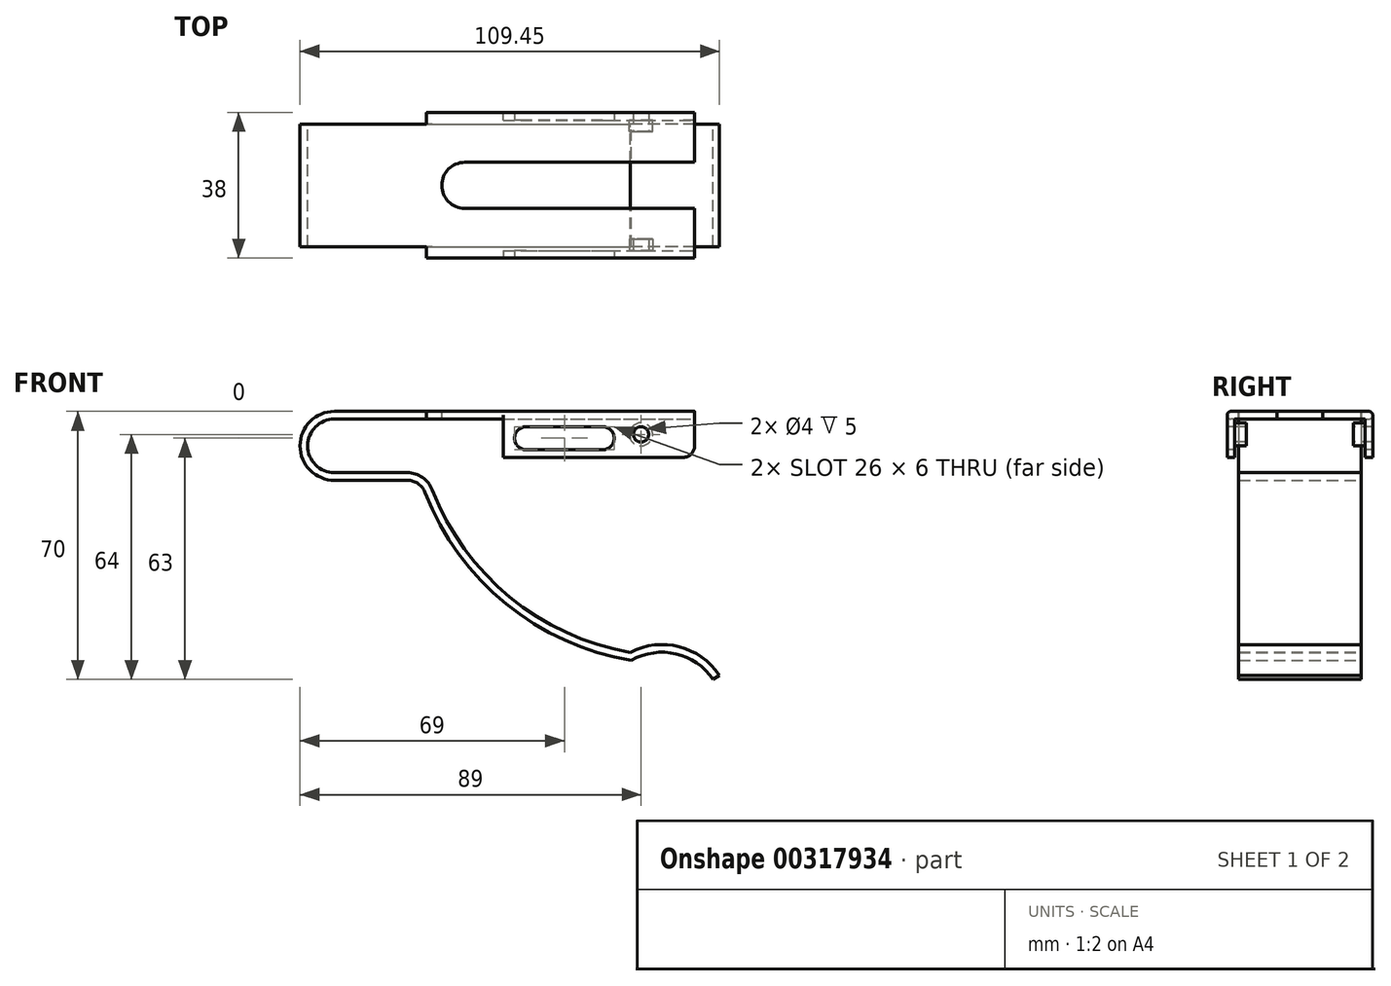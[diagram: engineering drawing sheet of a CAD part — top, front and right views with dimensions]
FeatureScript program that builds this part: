
annotation { "Feature Type Name" : "Feature", "Feature Type Description" : "" }
export const myFeature = defineFeature(function(context is Context, id is Id, definition is map)
    precondition{}
    {
        {
            var Q0;
            Q0=qCreatedBy(makeId("Front.planeOp"),FACE);
            var sketch = newSketch(context, id + "F0", { "sketchPlane" : qUnion([Q0])});
            skArc(sketch, "E0", {"start": v(0, 9) * mm, "mid": v(-9, 0) * mm, "end": v(0, -9) * mm});
            skLineSegment(sketch, "E1", {"start": v(0, 9) * mm, "end": v(94, 9) * mm});
            skLineSegment(sketch, "E2", {"start": v(0, -9) * mm, "end": v(19, -9) * mm});
            skArc(sketch, "E3", {"start": v(23.66, -12.2) * mm, "mid": v(44.77, -41.24) * mm, "end": v(77.5, -56) * mm});
            skArc(sketch, "E4", {"start": v(98.78, -61) * mm, "mid": v(89.13, -54.3) * mm, "end": v(77.5, -56) * mm});
            skPoint(sketch, "E5.visualSharp", {"position": v(22.52, -9) * mm});
            skArc(sketch, "E5.filletArc", {"start": v(23.66, -12.2) * mm, "mid": v(21.83, -9.88) * mm, "end": v(19, -9) * mm});
            skLineSegment(sketch, "E6.0", {"start": v(0, 7) * mm, "end": v(94, 7) * mm});
            skArc(sketch, "E6.1", {"start": v(0, 7) * mm, "mid": v(-7, 0) * mm, "end": v(0, -7) * mm});
            skArc(sketch, "E6.2", {"start": v(100.45, -59.9) * mm, "mid": v(89.94, -52.44) * mm, "end": v(77.15, -53.91) * mm});
            skArc(sketch, "E6.3", {"start": v(25.53, -11.47) * mm, "mid": v(45.77, -39.47) * mm, "end": v(77.15, -53.91) * mm});
            skArc(sketch, "E6.4", {"start": v(25.53, -11.47) * mm, "mid": v(22.96, -8.23) * mm, "end": v(19, -7) * mm});
            skLineSegment(sketch, "E6.5", {"start": v(0, -7) * mm, "end": v(19, -7) * mm});
            skLineSegment(sketch, "E7", {"start": v(94, 9) * mm, "end": v(94, 7) * mm});
            skLineSegment(sketch, "E8", {"start": v(100.45, -59.9) * mm, "end": v(98.78, -61) * mm});
            skSolve(sketch);
        }
        {
            var Q0;
            Q0=qSketchRegion(id+"F0",true);
            extrude(context, id + "F1", {"entities" : qUnion([Q0]), "depth" : 16 * mm});
        }
        {
            var Q0;
            Q0=makeQuery(id+"F1.opExtrude","SWEPT_FACE",FACE,{"disambiguationData":[OSD([sQuery(id+"F0.wireOp",EDGE,"E1")])]});
            var sketch = newSketch(context, id + "F2", { "sketchPlane" : qUnion([Q0])});
            skLineSegment(sketch, "E9.bottom", {"start": v(79.88, -16) * mm, "end": v(24, -16) * mm});
            skLineSegment(sketch, "E9.top", {"start": v(94, -19) * mm, "end": v(24, -19) * mm});
            skLineSegment(sketch, "E9.left", {"start": v(94, -16) * mm, "end": v(94, -19) * mm});
            skLineSegment(sketch, "E9.right", {"start": v(24, -16) * mm, "end": v(24, -19) * mm});
            skLineSegment(sketch, "E10.top", {"start": v(94, -10.87) * mm, "end": v(79.88, -10.87) * mm});
            skLineSegment(sketch, "E10.left", {"start": v(94, -16) * mm, "end": v(94, -10.87) * mm});
            skLineSegment(sketch, "E10.right", {"start": v(79.88, -16) * mm, "end": v(79.88, -10.87) * mm});
            skSolve(sketch);
        }
        {
            var Q0;
            Q0=makeQuery(id+"F2.imprint","IMPRINT",FACE,{"disambiguationData":[TD([[makeQuery(id+"F2.imprint","IMPRINT",EDGE,{"derivedFrom":sQuery(id+"F2.wireOp",EDGE,"E10.top")}),1.0]])]});
            var Q1;
            {var subQ1=sQuery(id+"F2.wireOp",EDGE,"E9.bottom");Q1=makeQuery(id+"F2.imprint","IMPRINT",FACE,{"disambiguationData":[TD([[makeQuery(id+"F2.imprint","IMPRINT",EDGE,{"derivedFrom":subQ1}),-1.0]])]});}
            extrude(context, id + "F3", {"entities" : qUnion([Q0, Q1]), "operationType" : NewBodyOperationType.ADD, "oppositeDirection" : true, "depth" : 2 * mm});
        }
        {
            var Q0;
            Q0=makeQuery(id+"F3.opExtrude","SWEPT_FACE",FACE,{"disambiguationData":[OSD([sQuery(id+"F2.wireOp",EDGE,"E9.top")])]});
            var sketch = newSketch(context, id + "F4", { "sketchPlane" : qUnion([Q0])});
            skPoint(sketch, "E11", {"position": v(94, -3) * mm});
            skPoint(sketch, "E11.positionSnap0", {"position": v(94, 8) * mm});
            skPoint(sketch, "E12", {"position": v(94, 9) * mm});
            skLineSegment(sketch, "E13.bottom", {"start": v(44, 9) * mm, "end": v(94, 9) * mm});
            skLineSegment(sketch, "E13.top", {"start": v(44, -3) * mm, "end": v(94, -3) * mm});
            skLineSegment(sketch, "E13.left", {"start": v(44, 9) * mm, "end": v(44, -3) * mm});
            skLineSegment(sketch, "E13.right", {"start": v(94, 9) * mm, "end": v(94, -3) * mm});
            skSolve(sketch);
        }
        {
            var Q0;
            Q0=qSketchRegion(id+"F4",true);
            extrude(context, id + "F5", {"entities" : qUnion([Q0]), "operationType" : NewBodyOperationType.ADD, "oppositeDirection" : true, "depth" : 2 * mm});
        }
        {
            var Q0;
            Q0=makeQuery(id+"F3.opExtrude","CAP_EDGE",EDGE,{"disambiguationData":[OSD([sQuery(id+"F2.wireOp",EDGE,"E9.top")])],"isStart":true});
            var Q1;
            Q1=makeQuery(id+"F3.opExtrude","CAP_EDGE",EDGE,{"disambiguationData":[OSD([sQuery(id+"F2.wireOp",EDGE,"E9.top")])],"isStart":false});
            fillet(context, id + "F6", {"entities" : qUnion([Q0, Q1]), "radius" : 1 * mm, "tangentPropagation" : true, "allowEdgeOverflow" : false});
        }
        {
            var Q0;
            Q0=makeQuery(id+"F1.opExtrude","SWEPT_BODY",BODY,{"disambiguationData":[OSD([sQuery(id+"F0.wireOp",EDGE,"E0"),sQuery(id+"F0.wireOp",EDGE,"E1"),sQuery(id+"F0.wireOp",EDGE,"E2"),sQuery(id+"F0.wireOp",EDGE,"E3"),sQuery(id+"F0.wireOp",EDGE,"E4"),sQuery(id+"F0.wireOp",EDGE,"E5.filletArc"),sQuery(id+"F0.wireOp",EDGE,"E6.0"),sQuery(id+"F0.wireOp",EDGE,"E6.1"),sQuery(id+"F0.wireOp",EDGE,"E6.2"),sQuery(id+"F0.wireOp",EDGE,"E6.3"),sQuery(id+"F0.wireOp",EDGE,"E6.4"),sQuery(id+"F0.wireOp",EDGE,"E6.5"),sQuery(id+"F0.wireOp",EDGE,"E7"),sQuery(id+"F0.wireOp",EDGE,"E8")])]});
            var Q1;
            Q1=qCreatedBy(makeId("Front.planeOp"),FACE);
            mirror(context, id + "F7", {"operationType" : NewBodyOperationType.ADD, "entities" : qUnion([Q0]), "mirrorPlane" : qUnion([Q1])});
        }
        {
            var Q0;
            {var subQ0=makeQuery(id+"F3.boolean.opBoolean","MERGE",FACE,{"derivedFrom":[makeQuery(id+"F1.opExtrude","SWEPT_FACE",FACE,{"disambiguationData":[OSD([sQuery(id+"F0.wireOp",EDGE,"E1")])]}),makeQuery(id+"F3.opExtrude","CAP_FACE",FACE,{"disambiguationData":[OSD([sQuery(id+"F2.wireOp",EDGE,"E9.bottom"),sQuery(id+"F2.wireOp",EDGE,"E9.top"),sQuery(id+"F2.wireOp",EDGE,"E9.left"),sQuery(id+"F2.wireOp",EDGE,"E9.right"),sQuery(id+"F2.wireOp",EDGE,"E10.top"),sQuery(id+"F2.wireOp",EDGE,"E10.left"),sQuery(id+"F2.wireOp",EDGE,"E10.right")])],"isStart":true})]});Q0=makeQuery(id+"F7.boolean.opBoolean","MERGE",FACE,{"derivedFrom":[subQ0,makeQuery(id+"F7.opPattern","COPY",FACE,{"derivedFrom":subQ0,"instanceName":"1"})]});}
            var sketch = newSketch(context, id + "F8", { "sketchPlane" : qUnion([Q0])});
            skPoint(sketch, "E14", {"position": v(0, 0) * mm});
            skArc(sketch, "E15", {"start": v(34, 6) * mm, "mid": v(28, 0) * mm, "end": v(34, -6) * mm});
            skPoint(sketch, "E16", {"position": v(34, 6) * mm});
            skLineSegment(sketch, "E17", {"start": v(34, 6) * mm, "end": v(94, 6) * mm});
            skPoint(sketch, "E18", {"position": v(34, -6) * mm});
            skLineSegment(sketch, "E19", {"start": v(94, 6) * mm, "end": v(94, -6) * mm});
            skLineSegment(sketch, "E20", {"start": v(94, -6) * mm, "end": v(34, -6) * mm});
            skSolve(sketch);
        }
        {
            var Q0;
            Q0=qSketchRegion(id+"F8",true);
            extrude(context, id + "F9", {"entities" : qUnion([Q0]), "operationType" : NewBodyOperationType.REMOVE, "oppositeDirection" : true, "depth" : 2 * mm});
        }
        {
            var Q0;
            Q0=makeQuery(id+"F5.boolean.opBoolean","MERGE",FACE,{"derivedFrom":[makeQuery(id+"F3.opExtrude","SWEPT_FACE",FACE,{"disambiguationData":[OSD([sQuery(id+"F2.wireOp",EDGE,"E9.top")])]}),makeQuery(id+"F5.opExtrude","CAP_FACE",FACE,{"disambiguationData":[OSD([sQuery(id+"F4.wireOp",EDGE,"E13.bottom"),sQuery(id+"F4.wireOp",EDGE,"E13.top"),sQuery(id+"F4.wireOp",EDGE,"E13.left"),sQuery(id+"F4.wireOp",EDGE,"E13.right")])],"isStart":true})]});
            var sketch = newSketch(context, id + "F10", { "sketchPlane" : qUnion([Q0])});
            skLineSegment(sketch, "E21", {"start": v(50, 2) * mm, "end": v(70, 2) * mm});
            skArc(sketch, "E22.0.startCap", {"start": v(50, -1) * mm, "mid": v(47, 2) * mm, "end": v(50, 5) * mm});
            skArc(sketch, "E22.0.endCap", {"start": v(70, 5) * mm, "mid": v(73, 2) * mm, "end": v(70, -1) * mm});
            skLineSegment(sketch, "E22.0.left", {"start": v(50, 5) * mm, "end": v(70, 5) * mm});
            skLineSegment(sketch, "E22.0.right", {"start": v(50, -1) * mm, "end": v(70, -1) * mm});
            skSolve(sketch);
        }
        {
            var Q0;
            Q0=qSketchRegion(id+"F10",true);
            extrude(context, id + "F11", {"entities" : qUnion([Q0]), "operationType" : NewBodyOperationType.ADD, "endBound" : BoundingType.THROUGH_ALL, "depth" : 25 * mm});
        }
        {
            var Q0;
            Q0=makeQuery(id+"F5.boolean.opBoolean","MERGE",FACE,{"derivedFrom":[makeQuery(id+"F3.opExtrude","SWEPT_FACE",FACE,{"disambiguationData":[OSD([sQuery(id+"F2.wireOp",EDGE,"E9.top")])]}),makeQuery(id+"F5.opExtrude","CAP_FACE",FACE,{"disambiguationData":[OSD([sQuery(id+"F4.wireOp",EDGE,"E13.bottom"),sQuery(id+"F4.wireOp",EDGE,"E13.top"),sQuery(id+"F4.wireOp",EDGE,"E13.left"),sQuery(id+"F4.wireOp",EDGE,"E13.right")])],"isStart":true})]});
            var sketch = newSketch(context, id + "F12", { "sketchPlane" : qUnion([Q0])});
            skPoint(sketch, "E23", {"position": v(80, 3) * mm});
            skPoint(sketch, "E23.positionSnap0", {"position": v(94, 2.5) * mm});
            skSolve(sketch);
        }
        {
            var Q0;
            Q0=sQuery(id+"F12.wireOp",VERTEX,"E23");
            var Q1;
            Q1=makeQuery(id+"F1.opExtrude","SWEPT_BODY",BODY,{"disambiguationData":[OSD([sQuery(id+"F0.wireOp",EDGE,"E0"),sQuery(id+"F0.wireOp",EDGE,"E1"),sQuery(id+"F0.wireOp",EDGE,"E2"),sQuery(id+"F0.wireOp",EDGE,"E3"),sQuery(id+"F0.wireOp",EDGE,"E4"),sQuery(id+"F0.wireOp",EDGE,"E5.filletArc"),sQuery(id+"F0.wireOp",EDGE,"E6.0"),sQuery(id+"F0.wireOp",EDGE,"E6.1"),sQuery(id+"F0.wireOp",EDGE,"E6.2"),sQuery(id+"F0.wireOp",EDGE,"E6.3"),sQuery(id+"F0.wireOp",EDGE,"E6.4"),sQuery(id+"F0.wireOp",EDGE,"E6.5"),sQuery(id+"F0.wireOp",EDGE,"E7"),sQuery(id+"F0.wireOp",EDGE,"E8")])]});
            hole(context, id + "F13", {"style" : HoleStyle.SIMPLE, "endStyle" : HoleEndStyle.THROUGH, "holeDiameter" : 4 * mm, "locations" : qUnion([Q0]), "scope" : qUnion([Q1]), "isTappedThrough" : true});
        }
        {
            var Q0;
            Q0=makeQuery(id+"F5.boolean.opBoolean","MERGE",FACE,{"derivedFrom":[makeQuery(id+"F3.opExtrude","SWEPT_FACE",FACE,{"disambiguationData":[OSD([sQuery(id+"F2.wireOp",EDGE,"E9.top")])]}),makeQuery(id+"F5.opExtrude","CAP_FACE",FACE,{"disambiguationData":[OSD([sQuery(id+"F4.wireOp",EDGE,"E13.bottom"),sQuery(id+"F4.wireOp",EDGE,"E13.top"),sQuery(id+"F4.wireOp",EDGE,"E13.left"),sQuery(id+"F4.wireOp",EDGE,"E13.right")])],"isStart":true})]});
            var sketch = newSketch(context, id + "F14", { "sketchPlane" : qUnion([Q0])});
            skCircle(sketch, "E24.0", {"center": v(80, 3) * mm, "radius": 2 * mm});
            skCircle(sketch, "E25.0", {"center": v(80, 3) * mm, "radius": 3 * mm});
            skSolve(sketch);
        }
        {
            var Q0;
            Q0=qSketchRegion(id+"F14",true);
            extrude(context, id + "F15", {"entities" : qUnion([Q0]), "operationType" : NewBodyOperationType.ADD, "oppositeDirection" : true, "depth" : 5 * mm});
        }
        {
            var Q0;
            Q0=makeQuery(id+"F11.opExtrude","CAP_FACE",FACE,{"disambiguationData":[OSD([sQuery(id+"F10.wireOp",EDGE,"E22.0.startCap"),sQuery(id+"F10.wireOp",EDGE,"E22.0.endCap"),sQuery(id+"F10.wireOp",EDGE,"E22.0.left"),sQuery(id+"F10.wireOp",EDGE,"E22.0.right")])],"isStart":false});
            extrude(context, id + "F16", {"entities" : qUnion([Q0]), "operationType" : NewBodyOperationType.REMOVE, "endBound" : BoundingType.THROUGH_ALL, "oppositeDirection" : true, "depth" : 25 * mm});
        }
        {
            var Q0;
            Q0=makeQuery(id+"F7.opPattern","COPY",FACE,{"derivedFrom":makeQuery(id+"F5.boolean.opBoolean","MERGE",FACE,{"derivedFrom":[makeQuery(id+"F3.opExtrude","SWEPT_FACE",FACE,{"disambiguationData":[OSD([sQuery(id+"F2.wireOp",EDGE,"E9.top")])]}),makeQuery(id+"F5.opExtrude","CAP_FACE",FACE,{"disambiguationData":[OSD([sQuery(id+"F4.wireOp",EDGE,"E13.bottom"),sQuery(id+"F4.wireOp",EDGE,"E13.top"),sQuery(id+"F4.wireOp",EDGE,"E13.left"),sQuery(id+"F4.wireOp",EDGE,"E13.right")])],"isStart":true})]}),"instanceName":"1"});
            var sketch = newSketch(context, id + "F17", { "sketchPlane" : qUnion([Q0])});
            skCircle(sketch, "E26.0", {"center": v(-80, 3) * mm, "radius": 3 * mm});
            skSolve(sketch);
        }
        {
            var Q0;
            Q0=makeQuery(id+"F17.imprint","IMPRINT",FACE,{"disambiguationData":[TD([[makeQuery(id+"F17.imprint","IMPRINT",EDGE,{"derivedFrom":sQuery(id+"F17.wireOp",EDGE,"E26.0")}),1.0]])]});
            extrude(context, id + "F18", {"entities" : qUnion([Q0]), "operationType" : NewBodyOperationType.ADD, "oppositeDirection" : true, "depth" : 5 * mm});
        }
        {
            var Q0;
            Q0=makeQuery(id+"F5.opExtrude","SWEPT_EDGE",EDGE,{"disambiguationData":[OSD([sQuery(id+"F4.wireOp",EDGE,"E13.top"),sQuery(id+"F4.wireOp",EDGE,"E13.right")])]});
            var Q1;
            Q1=makeQuery(id+"F7.opPattern","COPY",EDGE,{"derivedFrom":makeQuery(id+"F5.opExtrude","SWEPT_EDGE",EDGE,{"disambiguationData":[OSD([sQuery(id+"F4.wireOp",EDGE,"E13.top"),sQuery(id+"F4.wireOp",EDGE,"E13.right")])]}),"instanceName":"1"});
            fillet(context, id + "F19", {"entities" : qUnion([Q0, Q1]), "radius" : 3 * mm, "tangentPropagation" : true, "allowEdgeOverflow" : false});
        }
    });
